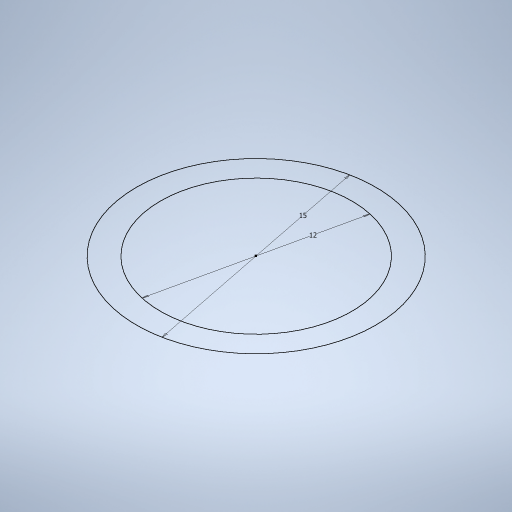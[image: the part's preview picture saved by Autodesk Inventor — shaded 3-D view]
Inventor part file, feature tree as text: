
AUTODESK INVENTOR PART (.ipt)
format: ipt  version: 2023 (Build 270158000, 158)  size: 220,160 bytes
history: native  units: mm
features: sketch x1
ambient origin geometry x8: Origin, YZ Plane, XZ Plane, XY Plane, X Axis, Y Axis, Z Axis, Center Point
feature tree (1):
  sketch  "Sketch1"  dims[d0=12.0mm d1=15.0mm]
